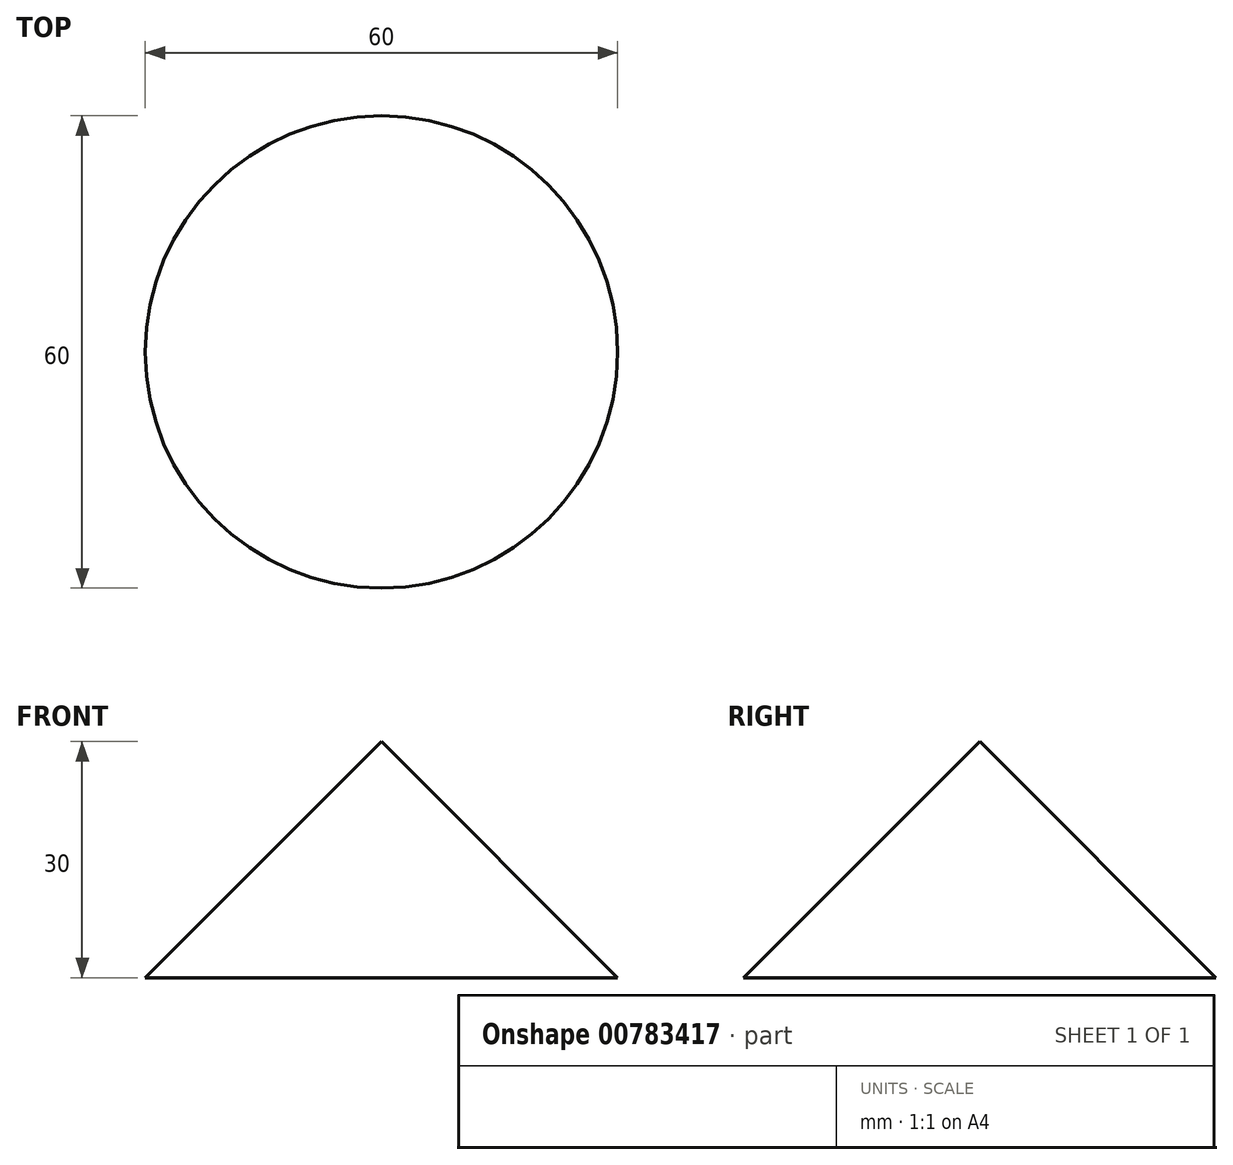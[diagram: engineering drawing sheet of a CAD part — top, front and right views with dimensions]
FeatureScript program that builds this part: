
annotation { "Feature Type Name" : "Feature", "Feature Type Description" : "" }
export const myFeature = defineFeature(function(context is Context, id is Id, definition is map)
    precondition{}
    {
        {
            var Q0;
            Q0=qCreatedBy(makeId("Front.planeOp"),FACE);
            var sketch = newSketch(context, id + "F0", { "sketchPlane" : qUnion([Q0])});
            skLineSegment(sketch, "E0", {"start": v(0, 0) * mm, "end": v(0, 30) * mm});
            skLineSegment(sketch, "E1", {"start": v(0, 30) * mm, "end": v(30, 0) * mm});
            skLineSegment(sketch, "E2", {"start": v(30, 0) * mm, "end": v(0, 0) * mm});
            skLineSegment(sketch, "E3", {"start": v(0, 0) * mm, "end": v(0, -14.29) * mm, "construction": true});
            skSolve(sketch);
        }
        {
            var Q0;
            Q0=makeQuery(id+"F0.imprint","IMPRINT",FACE,{"disambiguationData":[TD([[makeQuery(id+"F0.imprint","IMPRINT",EDGE,{"derivedFrom":sQuery(id+"F0.wireOp",EDGE,"E0")}),-1.0]])]});
            var Q1;
            Q1=sQuery(id+"F0.wireOp",EDGE,"E3");
            revolve(context, id + "F1", {"surfaceOperationType" : NewSurfaceOperationType.NEW, "entities" : qUnion([Q0]), "axis" : qUnion([Q1]), "revolveType" : RevolveType.FULL});
        }
    });
